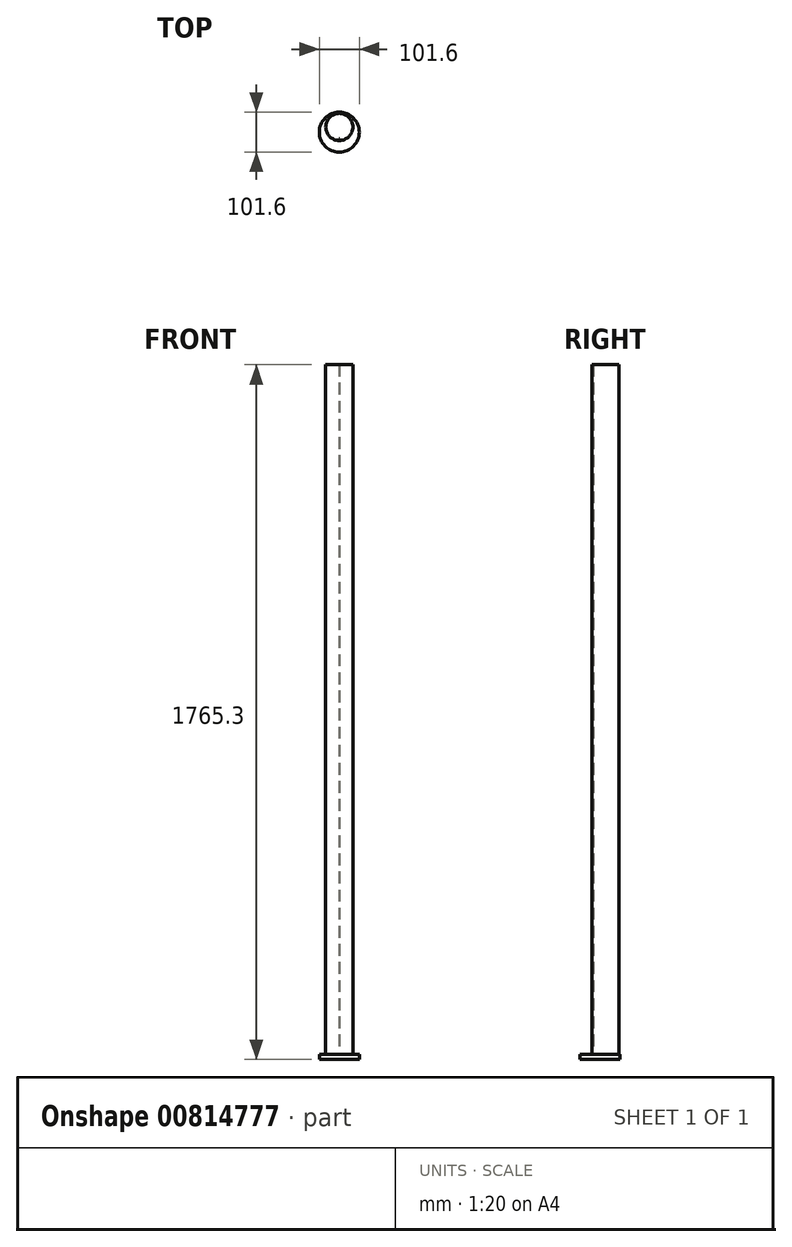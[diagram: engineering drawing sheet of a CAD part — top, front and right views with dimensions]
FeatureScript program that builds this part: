
annotation { "Feature Type Name" : "Feature", "Feature Type Description" : "" }
export const myFeature = defineFeature(function(context is Context, id is Id, definition is map)
    precondition{}
    {
        {
            var Q0;
            Q0=qCreatedBy(makeId("Top.planeOp"),FACE);
            var sketch = newSketch(context, id + "F0", { "sketchPlane" : qUnion([Q0])});
            skCircle(sketch, "E0", {"center": v(0, 0) * mm, "radius": 50.8 * mm});
            skSolve(sketch);
        }
        {
            var Q0;
            Q0=makeQuery(id+"F0.imprint","IMPRINT",FACE,{"disambiguationData":[TD([[makeQuery(id+"F0.imprint","IMPRINT",EDGE,{"derivedFrom":sQuery(id+"F0.wireOp",EDGE,"E0")}),1.0]])]});
            extrude(context, id + "F1", {"entities" : qUnion([Q0]), "depth" : 12.7 * mm, "offsetDistance" : 25.4 * mm});
        }
        {
            var Q0;
            Q0=makeQuery(id+"F1.opExtrude","CAP_FACE",FACE,{"disambiguationData":[OSD([sQuery(id+"F0.wireOp",EDGE,"E0")])],"isStart":false});
            var sketch = newSketch(context, id + "F2", { "sketchPlane" : qUnion([Q0])});
            skCircle(sketch, "E1", {"center": v(0, 13.23) * mm, "radius": 34.48 * mm});
            skCircle(sketch, "E2", {"center": v(-12.7, -18.82) * mm, "radius": 12.87 * mm});
            skCircle(sketch, "E3", {"center": v(12.7, -18.82) * mm, "radius": 12.88 * mm});
            skSolve(sketch);
        }
        {
            var Q0;
            {var subQ0=sQuery(id+"F2.wireOp",EDGE,"E2");var subQ1=sQuery(id+"F2.wireOp",EDGE,"E1");var subQ2=makeQuery(id+"F2.imprint","INTERSECT",VERTEX,{"disambiguationData":[OD(0.0)],"derivedFrom":[subQ1,subQ0]});Q0=makeQuery(id+"F2.imprint","IMPRINT",FACE,{"disambiguationData":[TD([[makeQuery(id+"F2.imprint","IMPRINT",EDGE,{"disambiguationData":[TD([[subQ2,-1.0]])],"derivedFrom":subQ1}),1.0]])]});}
            var Q1;
            {var subQ0=sQuery(id+"F2.wireOp",EDGE,"E2");var subQ1=sQuery(id+"F2.wireOp",EDGE,"E1");var subQ2=makeQuery(id+"F2.imprint","INTERSECT",VERTEX,{"disambiguationData":[OD(1.0)],"derivedFrom":[subQ1,subQ0]});Q1=makeQuery(id+"F2.imprint","IMPRINT",FACE,{"disambiguationData":[TD([[makeQuery(id+"F2.imprint","IMPRINT",EDGE,{"disambiguationData":[TD([[subQ2,1.0]])],"derivedFrom":subQ1}),1.0]])]});}
            var Q2;
            {var subQ0=sQuery(id+"F2.wireOp",EDGE,"E2");var subQ1=sQuery(id+"F2.wireOp",EDGE,"E1");var subQ2=makeQuery(id+"F2.imprint","INTERSECT",VERTEX,{"disambiguationData":[OD(0.0)],"derivedFrom":[subQ1,subQ0]});Q2=makeQuery(id+"F2.imprint","IMPRINT",FACE,{"disambiguationData":[TD([[makeQuery(id+"F2.imprint","IMPRINT",EDGE,{"disambiguationData":[TD([[subQ2,1.0]])],"derivedFrom":subQ1}),1.0]])]});}
            var Q3;
            {var subQ0=sQuery(id+"F2.wireOp",EDGE,"E3");var subQ1=sQuery(id+"F2.wireOp",EDGE,"E1");var subQ2=makeQuery(id+"F2.imprint","INTERSECT",VERTEX,{"disambiguationData":[OD(0.0)],"derivedFrom":[subQ1,subQ0]});Q3=makeQuery(id+"F2.imprint","IMPRINT",FACE,{"disambiguationData":[TD([[makeQuery(id+"F2.imprint","IMPRINT",EDGE,{"disambiguationData":[TD([[subQ2,-1.0]])],"derivedFrom":subQ1}),1.0]])]});}
            extrude(context, id + "F3", {"entities" : qUnion([Q0, Q1, Q2, Q3]), "operationType" : NewBodyOperationType.ADD, "depth" : 1752.6 * mm, "offsetDistance" : 25.4 * mm});
        }
    });
